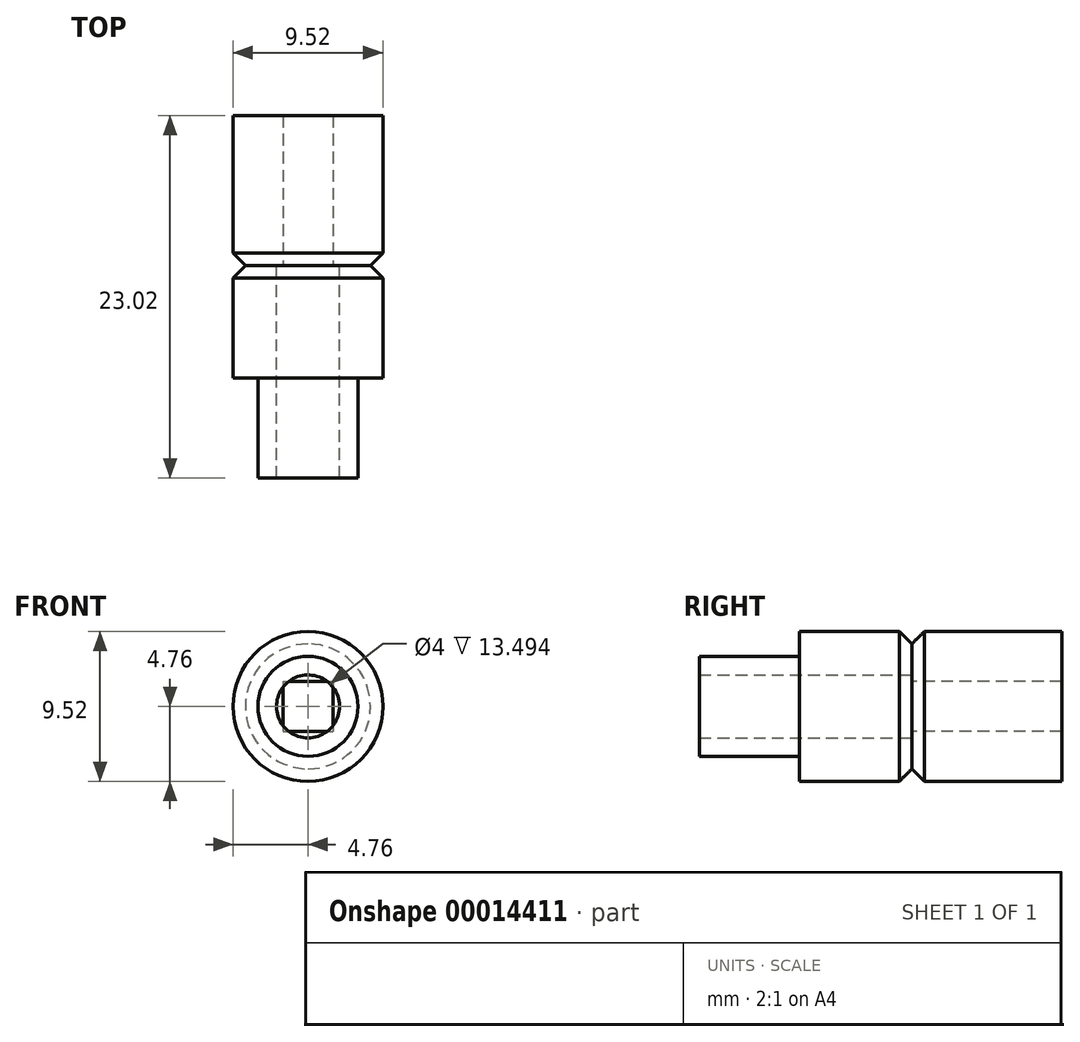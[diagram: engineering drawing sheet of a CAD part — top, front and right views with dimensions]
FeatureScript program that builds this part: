
annotation { "Feature Type Name" : "Feature", "Feature Type Description" : "" }
export const myFeature = defineFeature(function(context is Context, id is Id, definition is map)
    precondition{}
    {
        {
            var Q0;
            Q0=qCreatedBy(makeId("Front.planeOp"),FACE);
            var sketch = newSketch(context, id + "F0", { "sketchPlane" : qUnion([Q0])});
            skCircle(sketch, "E0", {"center": v(0, 0) * mm, "radius": 3.18 * mm});
            skSolve(sketch);
        }
        {
            var Q0;
            Q0=qSketchRegion(id+"F0",true);
            extrude(context, id + "F1", {"entities" : qUnion([Q0]), "depth" : 6.35 * mm});
        }
        {
            var Q0;
            Q0=qCreatedBy(makeId("Front.planeOp"),FACE);
            var sketch = newSketch(context, id + "F2", { "sketchPlane" : qUnion([Q0])});
            skCircle(sketch, "E1", {"center": v(0, 0) * mm, "radius": 4.76 * mm});
            skSolve(sketch);
        }
        {
            var Q0;
            Q0=qSketchRegion(id+"F2",true);
            extrude(context, id + "F3", {"entities" : qUnion([Q0]), "operationType" : NewBodyOperationType.ADD, "oppositeDirection" : true, "depth" : 7.14 * mm});
        }
        {
            var Q0;
            Q0=makeQuery(id+"F3.opExtrude","CAP_EDGE",EDGE,{"disambiguationData":[OSD([sQuery(id+"F2.wireOp",EDGE,"E1")])],"isStart":false});
            chamfer(context, id + "F4", {"entities" : qUnion([Q0]), "width" : 0.8 * mm, "tangentPropagation" : true});
        }
        {
            var Q0;
            Q0=makeQuery(id+"F3.opExtrude","CAP_FACE",FACE,{"disambiguationData":[OSD([sQuery(id+"F2.wireOp",EDGE,"E1")])],"isStart":false});
            var sketch = newSketch(context, id + "F5", { "sketchPlane" : qUnion([Q0])});
            skCircle(sketch, "E2", {"center": v(0, 0) * mm, "radius": 2 * mm});
            skSolve(sketch);
        }
        {
            var Q0;
            Q0=qSketchRegion(id+"F5",true);
            extrude(context, id + "F6", {"entities" : qUnion([Q0]), "operationType" : NewBodyOperationType.REMOVE, "endBound" : BoundingType.THROUGH_ALL, "oppositeDirection" : true, "depth" : 25.4 * mm});
        }
        {
            var Q0;
            Q0=makeQuery(id+"F3.opExtrude","CAP_FACE",FACE,{"disambiguationData":[OSD([sQuery(id+"F2.wireOp",EDGE,"E1")])],"isStart":false});
            var sketch = newSketch(context, id + "F7", { "sketchPlane" : qUnion([Q0])});
            skCircle(sketch, "E3", {"center": v(0, 0) * mm, "radius": 4.76 * mm});
            skLineSegment(sketch, "E4.rect.bottom", {"start": v(1.59, 1.59) * mm, "end": v(-1.59, 1.59) * mm});
            skLineSegment(sketch, "E4.rect.top", {"start": v(1.59, -1.59) * mm, "end": v(-1.59, -1.59) * mm});
            skLineSegment(sketch, "E4.rect.left", {"start": v(1.59, 1.59) * mm, "end": v(1.59, -1.59) * mm});
            skLineSegment(sketch, "E4.rect.right", {"start": v(-1.59, 1.59) * mm, "end": v(-1.59, -1.59) * mm});
            skSolve(sketch);
        }
        {
            var Q0;
            Q0=qSketchRegion(id+"F7",true);
            extrude(context, id + "F8", {"entities" : qUnion([Q0]), "operationType" : NewBodyOperationType.ADD, "depth" : 9.52 * mm});
        }
        {
            var Q0;
            Q0=makeQuery(id+"F8.opExtrude","CAP_EDGE",EDGE,{"disambiguationData":[OSD([sQuery(id+"F7.wireOp",EDGE,"E3")])],"isStart":true});
            chamfer(context, id + "F9", {"entities" : qUnion([Q0]), "width" : 0.8 * mm, "tangentPropagation" : true});
        }
    });
